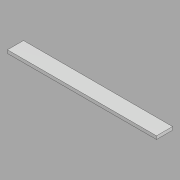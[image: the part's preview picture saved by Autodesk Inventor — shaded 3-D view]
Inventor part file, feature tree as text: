
AUTODESK INVENTOR PART (.ipt)
format: ipt  version: 2022.2 (Build 262287010, 287A)  size: 104,960 bytes
history: native  units: in
note: dims shown in document units (in); Inventor stores cm internally (conversion verified against a paired STEP export)
features: direct_edit x1, other x1, revolve x1
ambient origin geometry x8: Origin, YZ Plane, XZ Plane, XY Plane, X Axis, Y Axis, Z Axis, Center Point
bodies: Solid1 (feature_tree)
feature tree (3):
  direct_edit  "Direct Edit1"
  other  "R Vert rect jamb lower"
  revolve  "Rotate1"  [1 undecoded]
note: 1 required parameter value undecoded (feature->parameter linkage not recoverable at this tier; creation-order binding heuristic only, values carry confidence <= 0.55)
